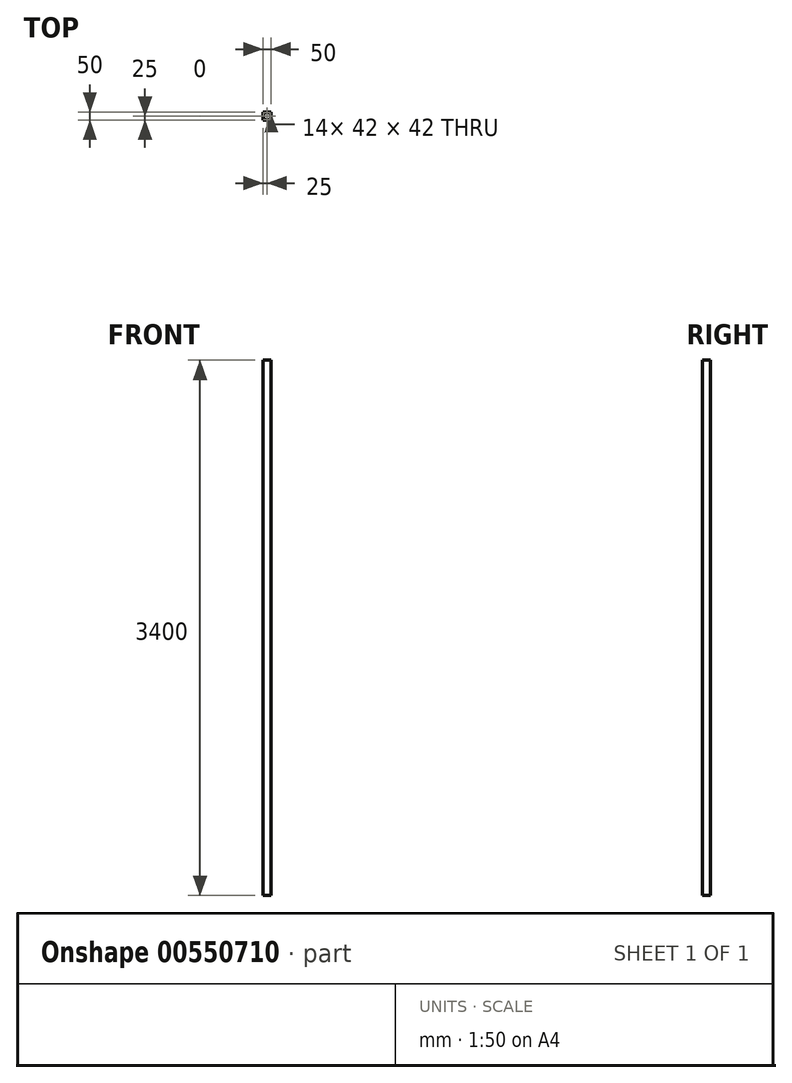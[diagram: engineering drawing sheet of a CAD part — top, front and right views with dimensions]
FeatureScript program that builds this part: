
annotation { "Feature Type Name" : "Feature", "Feature Type Description" : "" }
export const myFeature = defineFeature(function(context is Context, id is Id, definition is map)
    precondition{}
    {
        {
            var Q0;
            Q0=qCreatedBy(makeId("Top.planeOp"),FACE);
            var sketch = newSketch(context, id + "F0", { "sketchPlane" : qUnion([Q0])});
            skLineSegment(sketch, "E0.bottom", {"start": v(25, -25) * mm, "end": v(-25, -25) * mm});
            skLineSegment(sketch, "E0.top", {"start": v(25, 25) * mm, "end": v(-25, 25) * mm});
            skLineSegment(sketch, "E0.left", {"start": v(25, -25) * mm, "end": v(25, 25) * mm});
            skLineSegment(sketch, "E0.right", {"start": v(-25, -25) * mm, "end": v(-25, 25) * mm});
            skPoint(sketch, "E0.middle", {"position": v(0, 0) * mm});
            skLineSegment(sketch, "E1.bottom", {"start": v(21, -21) * mm, "end": v(-21, -21) * mm});
            skLineSegment(sketch, "E1.top", {"start": v(21, 21) * mm, "end": v(-21, 21) * mm});
            skLineSegment(sketch, "E1.left", {"start": v(21, -21) * mm, "end": v(21, 21) * mm});
            skLineSegment(sketch, "E1.right", {"start": v(-21, -21) * mm, "end": v(-21, 21) * mm});
            skSolve(sketch);
        }
        {
            var Q0;
            Q0=makeQuery(id+"F0.imprint","IMPRINT",FACE,{"disambiguationData":[TD([[makeQuery(id+"F0.imprint","IMPRINT",EDGE,{"derivedFrom":sQuery(id+"F0.wireOp",EDGE,"E0.bottom")}),-1.0]])]});
            extrude(context, id + "F1", {"entities" : qUnion([Q0]), "depth" : 3400 * mm, "offsetDistance" : 25 * mm});
        }
    });
